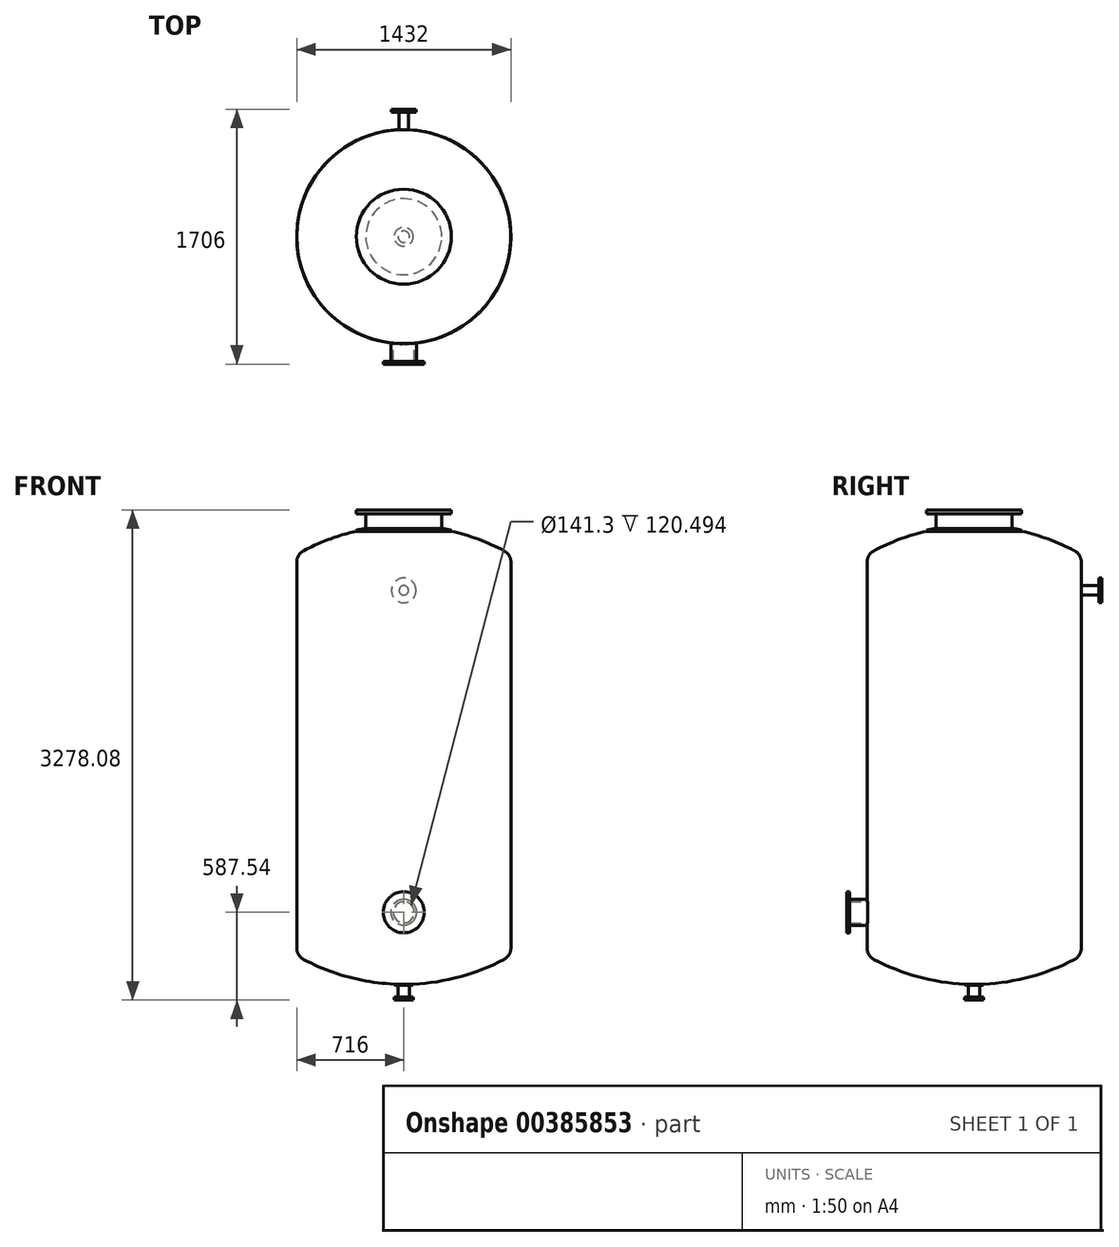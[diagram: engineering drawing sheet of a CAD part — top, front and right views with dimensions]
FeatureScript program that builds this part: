
annotation { "Feature Type Name" : "Feature", "Feature Type Description" : "" }
export const myFeature = defineFeature(function(context is Context, id is Id, definition is map)
    precondition{}
    {
        {
            var Q0;
            Q0=qCreatedBy(makeId("Front.planeOp"),FACE);
            var sketch = newSketch(context, id + "F0", { "sketchPlane" : qUnion([Q0])});
            skLineSegment(sketch, "E0", {"start": v(716, -1204.5) * mm, "end": v(716, 1204.5) * mm});
            skLineSegment(sketch, "E1.0", {"start": v(0, -1204.5) * mm, "end": v(0, 1204.5) * mm});
            skLineSegment(sketch, "E2", {"start": v(716, 1290.5) * mm, "end": v(630, 1290.5) * mm, "construction": true});
            skArc(sketch, "E3", {"start": v(716, 1290.5) * mm, "mid": v(703.68, 1334.85) * mm, "end": v(670.25, 1366.5) * mm});
            skArc(sketch, "E4", {"start": v(670.25, 1366.5) * mm, "mid": v(498.2, 1443.58) * mm, "end": v(317.5, 1497.4) * mm});
            skLineSegment(sketch, "E5", {"start": v(716, 1204.5) * mm, "end": v(716, 1290.5) * mm});
            skLineSegment(sketch, "E6", {"start": v(0, 1204.5) * mm, "end": v(0, 1533.04) * mm});
            skLineSegment(sketch, "E7", {"start": v(716, 0) * mm, "end": v(0, 0) * mm, "construction": true});
            skLineSegment(sketch, "E8.MirrorCS", {"start": v(0, -1204.5) * mm, "end": v(0, -1533.04) * mm});
            skArc(sketch, "E9.MirrorCS", {"start": v(670.25, -1366.5) * mm, "mid": v(376.05, -1482.78) * mm, "end": v(63.5, -1531.63) * mm});
            skLineSegment(sketch, "E10.MirrorCS", {"start": v(716, -1204.5) * mm, "end": v(716, -1290.5) * mm});
            skArc(sketch, "E11.MirrorCS", {"start": v(716, -1290.5) * mm, "mid": v(703.68, -1334.85) * mm, "end": v(670.25, -1366.5) * mm});
            skArc(sketch, "E12.0", {"start": v(317.5, 1503.55) * mm, "mid": v(285.82, 1510.35) * mm, "end": v(254, 1516.43) * mm});
            skArc(sketch, "E13.0", {"start": v(63.5, -1537.64) * mm, "mid": v(50.8, -1538.14) * mm, "end": v(38.1, -1538.53) * mm});
            skLineSegment(sketch, "E14", {"start": v(0, 1539.04) * mm, "end": v(0, 1533.04) * mm});
            skLineSegment(sketch, "E15", {"start": v(317.5, 1503.55) * mm, "end": v(317.5, 1497.4) * mm});
            skLineSegment(sketch, "E16", {"start": v(0, 1539.04) * mm, "end": v(0, 1639.04) * mm});
            skLineSegment(sketch, "E17", {"start": v(0, 1639.04) * mm, "end": v(317.5, 1639.04) * mm});
            skLineSegment(sketch, "E18", {"start": v(317.5, 1639.04) * mm, "end": v(317.5, 1613.64) * mm});
            skLineSegment(sketch, "E19", {"start": v(317.5, 1613.64) * mm, "end": v(254, 1613.64) * mm});
            skLineSegment(sketch, "E20", {"start": v(254, 1613.64) * mm, "end": v(254, 1516.43) * mm});
            skLineSegment(sketch, "E21", {"start": v(0, -1533.04) * mm, "end": v(0, -1539.04) * mm});
            skLineSegment(sketch, "E22", {"start": v(63.5, -1537.64) * mm, "end": v(63.5, -1531.63) * mm});
            skLineSegment(sketch, "E23", {"start": v(0, -1539.04) * mm, "end": v(0, -1639.04) * mm});
            skPoint(sketch, "E23.endSnap0", {"position": v(0, -1536.04) * mm});
            skLineSegment(sketch, "E24", {"start": v(0, -1639.04) * mm, "end": v(63.5, -1639.04) * mm});
            skLineSegment(sketch, "E25", {"start": v(63.5, -1639.04) * mm, "end": v(63.5, -1619.99) * mm});
            skLineSegment(sketch, "E26", {"start": v(63.5, -1619.99) * mm, "end": v(38.1, -1619.99) * mm});
            skLineSegment(sketch, "E27", {"start": v(38.1, -1619.99) * mm, "end": v(38.1, -1538.53) * mm});
            skPoint(sketch, "E28.orphan", {"position": v(0, -1533.04) * mm});
            skSolve(sketch);
        }
        {
            var Q0;
            Q0=makeQuery(id+"F0.imprint","IMPRINT",FACE,{"disambiguationData":[TD([[makeQuery(id+"F0.imprint","IMPRINT",EDGE,{"derivedFrom":sQuery(id+"F0.wireOp",EDGE,"E0")}),1.0]])]});
            var Q1;
            Q1=sQuery(id+"F0.wireOp",EDGE,"E1.0");
            revolve(context, id + "F1", {"entities" : qUnion([Q0]), "axis" : qUnion([Q1]), "revolveType" : RevolveType.FULL});
        }
        {
            var Q0;
            Q0=qCreatedBy(makeId("Front.planeOp"),FACE);
            var sketch = newSketch(context, id + "F2", { "sketchPlane" : qUnion([Q0])});
            skLineSegment(sketch, "E29", {"start": v(0, 0) * mm, "end": v(0, -1051.5) * mm, "construction": true});
            skCircle(sketch, "E30", {"center": v(0, -1051.5) * mm, "radius": 70.65 * mm});
            skCircle(sketch, "E31.0", {"center": v(0, -1051.5) * mm, "radius": 86.53 * mm});
            skLineSegment(sketch, "E32", {"start": v(0, 0) * mm, "end": v(0, 1101.5) * mm, "construction": true});
            skCircle(sketch, "E33", {"center": v(0, 1101.5) * mm, "radius": 31.65 * mm});
            skSolve(sketch);
        }
        {
            var Q0;
            Q0=makeQuery(id+"F2.imprint","IMPRINT",FACE,{"disambiguationData":[TD([[makeQuery(id+"F2.imprint","IMPRINT",EDGE,{"derivedFrom":sQuery(id+"F2.wireOp",EDGE,"E30")}),-1.0]])]});
            extrude(context, id + "F3", {"entities" : qUnion([Q0]), "operationType" : NewBodyOperationType.ADD, "depth" : 833 * mm});
        }
        {
            var Q0;
            Q0=makeQuery(id+"F3.opExtrude","CAP_FACE",FACE,{"disambiguationData":[OSD([sQuery(id+"F2.wireOp",EDGE,"E30"),sQuery(id+"F2.wireOp",EDGE,"E31.0")])],"isStart":false});
            var sketch = newSketch(context, id + "F4", { "sketchPlane" : qUnion([Q0])});
            skCircle(sketch, "E34", {"center": v(0, -1051.5) * mm, "radius": 137.33 * mm});
            skSolve(sketch);
        }
        {
            var Q0;
            Q0 = qSketchRegion(id + "F4", true);
            extrude(context, id + "F5", {"entities" : qUnion([Q0]), "operationType" : NewBodyOperationType.ADD, "depth" : 20 * mm});
        }
        {
            var Q0;
            Q0=makeQuery(id+"F2.imprint","IMPRINT",FACE,{"disambiguationData":[TD([[makeQuery(id+"F2.imprint","IMPRINT",EDGE,{"derivedFrom":sQuery(id+"F2.wireOp",EDGE,"E33")}),1.0]])]});
            extrude(context, id + "F6", {"entities" : qUnion([Q0]), "operationType" : NewBodyOperationType.ADD, "oppositeDirection" : true, "depth" : 833 * mm});
        }
        {
            var Q0;
            Q0=makeQuery(id+"F6.opExtrude","CAP_FACE",FACE,{"disambiguationData":[OSD([sQuery(id+"F2.wireOp",EDGE,"E33")])],"isStart":false});
            var sketch = newSketch(context, id + "F7", { "sketchPlane" : qUnion([Q0])});
            skCircle(sketch, "E35", {"center": v(0, 1101.5) * mm, "radius": 82.05 * mm});
            skSolve(sketch);
        }
        {
            var Q0;
            Q0 = qSketchRegion(id + "F7", true);
            extrude(context, id + "F8", {"entities" : qUnion([Q0]), "operationType" : NewBodyOperationType.ADD, "depth" : 20 * mm});
        }
    });
